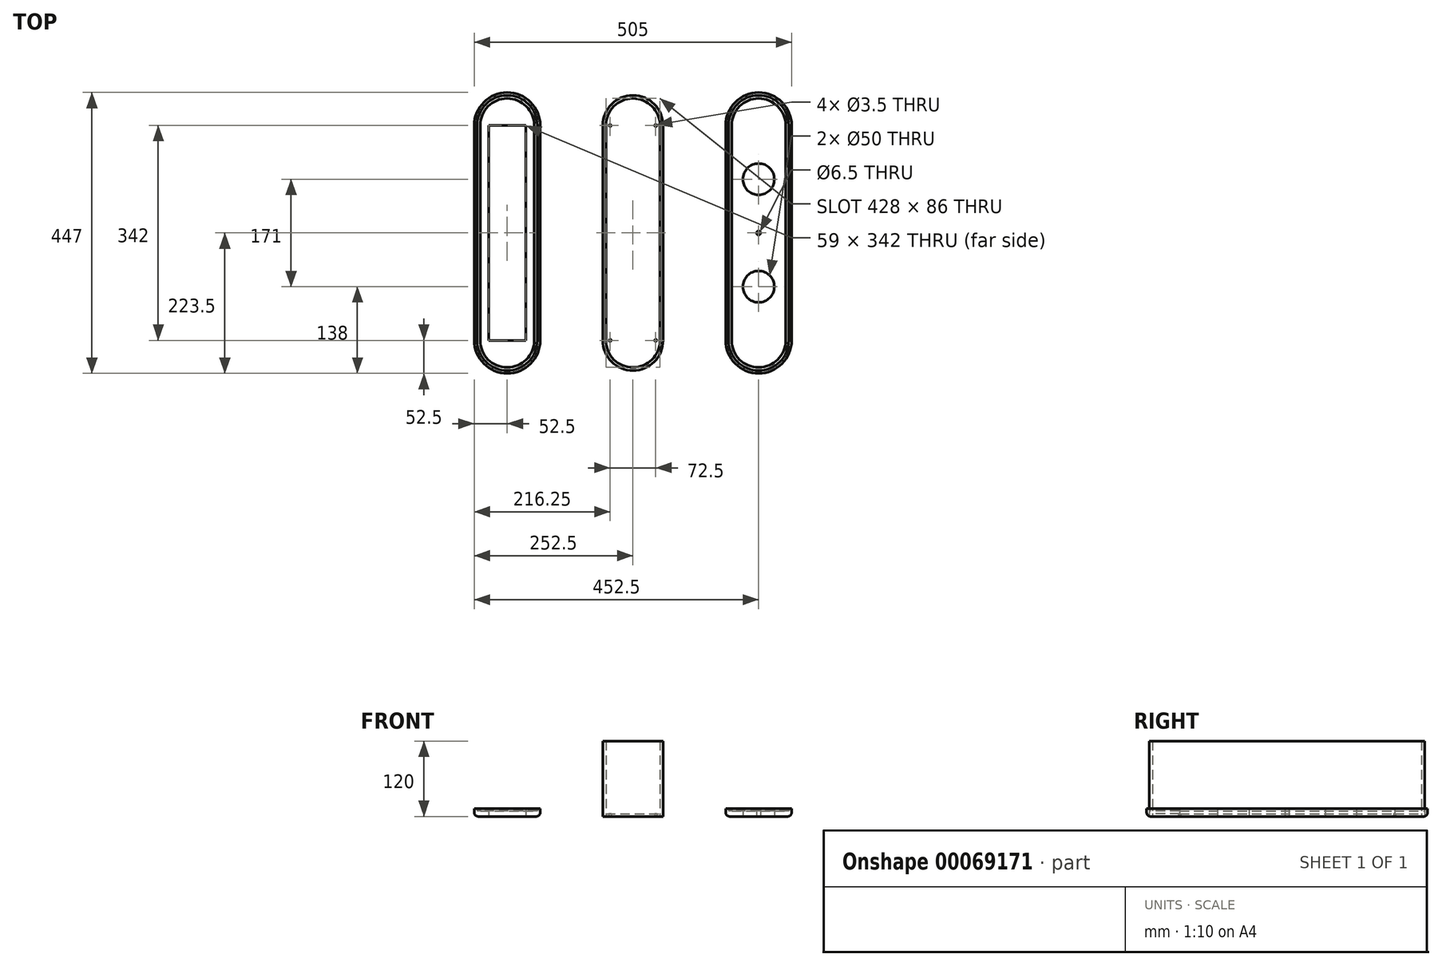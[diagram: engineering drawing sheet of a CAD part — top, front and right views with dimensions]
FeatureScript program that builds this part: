
annotation { "Feature Type Name" : "Feature", "Feature Type Description" : "" }
export const myFeature = defineFeature(function(context is Context, id is Id, definition is map)
    precondition{}
    {
        {
            assignVariable(context, id + "F0", {"name" : "MaterialThickness", "anyValue" : 12.7});
        }
        {
            assignVariable(context, id + "F1", {"name" : "SignHeight", "anyValue" : 120});
        }
        {
            assignVariable(context, id + "F2", {"name" : "SignThickness", "anyValue" : 4.5});
        }
        {
            var Q0;
            Q0=qCreatedBy(makeId("Top.planeOp"),FACE);
            var sketch = newSketch(context, id + "F3", { "sketchPlane" : qUnion([Q0])});
            skLineSegment(sketch, "E0", {"start": v(0, 0) * mm, "end": v(105, 0) * mm, "construction": true});
            skLineSegment(sketch, "E1", {"start": v(105, 0) * mm, "end": v(105, 171) * mm});
            skLineSegment(sketch, "E2", {"start": v(0, 0) * mm, "end": v(0, 171) * mm});
            skArc(sketch, "E3", {"start": v(105, 171) * mm, "mid": v(52.5, 223.5) * mm, "end": v(0, 171) * mm});
            skPoint(sketch, "E3.centerSnap0", {"position": v(52.5, 0) * mm});
            skLineSegment(sketch, "E4.0", {"start": v(100.5, 0) * mm, "end": v(100.5, 171) * mm});
            skArc(sketch, "E4.1", {"start": v(100.5, 171) * mm, "mid": v(52.5, 219) * mm, "end": v(4.5, 171) * mm});
            skLineSegment(sketch, "E4.2", {"start": v(4.5, 0) * mm, "end": v(4.5, 171) * mm});
            skLineSegment(sketch, "E5.0", {"start": v(9.5, 0) * mm, "end": v(9.5, 171) * mm});
            skArc(sketch, "E5.1", {"start": v(95.5, 171) * mm, "mid": v(52.5, 214) * mm, "end": v(9.5, 171) * mm});
            skLineSegment(sketch, "E5.2", {"start": v(95.5, 0) * mm, "end": v(95.5, 171) * mm});
            skArc(sketch, "E6.MirrorCS", {"start": v(95.5, -171) * mm, "mid": v(52.5, -214) * mm, "end": v(9.5, -171) * mm});
            skLineSegment(sketch, "E7.MirrorCS", {"start": v(105, 0) * mm, "end": v(105, -171) * mm});
            skArc(sketch, "E8.MirrorCS", {"start": v(100.5, -171) * mm, "mid": v(52.5, -219) * mm, "end": v(4.5, -171) * mm});
            skLineSegment(sketch, "E9.MirrorCS", {"start": v(4.5, 0) * mm, "end": v(4.5, -171) * mm});
            skLineSegment(sketch, "E10.MirrorCS", {"start": v(0, 0) * mm, "end": v(0, -171) * mm});
            skLineSegment(sketch, "E11.MirrorCS", {"start": v(9.5, 0) * mm, "end": v(9.5, -171) * mm});
            skArc(sketch, "E12.MirrorCS", {"start": v(105, -171) * mm, "mid": v(52.5, -223.5) * mm, "end": v(0, -171) * mm});
            skLineSegment(sketch, "E13.MirrorCS", {"start": v(95.5, 0) * mm, "end": v(95.5, -171) * mm});
            skLineSegment(sketch, "E14.MirrorCS", {"start": v(100.5, 0) * mm, "end": v(100.5, -171) * mm});
            skLineSegment(sketch, "E15", {"start": v(52.5, 171) * mm, "end": v(52.5, -171) * mm, "construction": true});
            skPoint(sketch, "E16", {"position": v(52.5, 85.5) * mm});
            skPoint(sketch, "E17.MirrorP", {"position": v(52.5, -85.5) * mm});
            skLineSegment(sketch, "E18.rect.bottom", {"start": v(82, 171) * mm, "end": v(23, 171) * mm});
            skLineSegment(sketch, "E18.rect.top", {"start": v(82, -171) * mm, "end": v(23, -171) * mm});
            skLineSegment(sketch, "E18.rect.left", {"start": v(82, 171) * mm, "end": v(82, -171) * mm});
            skLineSegment(sketch, "E18.rect.right", {"start": v(23, 171) * mm, "end": v(23, -171) * mm});
            skPoint(sketch, "E19", {"position": v(16.25, -171) * mm});
            skPoint(sketch, "E20.MirrorP", {"position": v(88.75, -171) * mm});
            skPoint(sketch, "E21.MirrorP", {"position": v(88.75, 171) * mm});
            skPoint(sketch, "E22.MirrorP", {"position": v(16.25, 171) * mm});
            skSolve(sketch);
        }
        {
            var Q0;
            {var subQ0=sQuery(id+"F3.wireOp",EDGE,"S4vBLkRr-qZBK-nAqC-RG6z-cKJkzYe95XTT");Q0=makeQuery(id+"F3.imprint","IMPRINT",FACE,{"disambiguationData":[TD([[makeQuery(id+"F3.imprint","IMPRINT",EDGE,{"derivedFrom":subQ0}),1.0]])]});}
            var Q1;
            {var subQ0=sQuery(id+"F3.wireOp",EDGE,"zH33Oyk7-acCO-qxZw-FpOp-6ZJnxs5qB4Y2");Q1=makeQuery(id+"F3.imprint","IMPRINT",FACE,{"disambiguationData":[TD([[makeQuery(id+"F3.imprint","IMPRINT",EDGE,{"derivedFrom":subQ0}),-1.0]])]});}
            var Q2;
            {var subQ0=sQuery(id+"F3.wireOp",EDGE,"VhilzIQP-kfQW-MNlP-IUHr-LsH6QfZYn0pK");Q2=makeQuery(id+"F3.imprint","IMPRINT",FACE,{"disambiguationData":[TD([[makeQuery(id+"F3.imprint","IMPRINT",EDGE,{"derivedFrom":subQ0}),1.0]])]});}
            var Q3;
            {var subQ4=sQuery(id+"F3.wireOp",EDGE,"E3");Q3=makeQuery(id+"F3.imprint","IMPRINT",FACE,{"disambiguationData":[TD([[makeQuery(id+"F3.imprint","IMPRINT",EDGE,{"derivedFrom":subQ4}),1.0]])]});}
            var Q4;
            Q4=makeQuery(id+"F3.imprint","IMPRINT",FACE,{"disambiguationData":[TD([[makeQuery(id+"F3.imprint","IMPRINT",EDGE,{"derivedFrom":sQuery(id+"F3.wireOp",EDGE,"E18.rect.bottom")}),1.0]])]});
            var Q5;
            Q5=makeQuery(id+"F3.imprint","IMPRINT",FACE,{"disambiguationData":[TD([[makeQuery(id+"F3.imprint","IMPRINT",EDGE,{"derivedFrom":sQuery(id+"F3.wireOp",EDGE,"E18.rect.bottom")}),-1.0]])]});
            var Q6;
            Q6=makeQuery(id+"F3.imprint","IMPRINT",FACE,{"disambiguationData":[TD([[makeQuery(id+"F3.imprint","IMPRINT",EDGE,{"derivedFrom":sQuery(id+"F3.wireOp",EDGE,"E5.0")}),-1.0]])]});
            extrude(context, id + "F4", {"entities" : qUnion([Q0, Q1, Q2, Q3, Q4, Q5, Q6]), "depth" : (getVariable(context, 'MaterialThickness')) * mm});
        }
        {
            var Q0;
            {var subQ0=sQuery(id+"F3.wireOp",EDGE,"yTFAeiCs-v25R-ZgTO-i8Xo-Mo7MgQb8BnxG");Q0=makeQuery(id+"F3.imprint","IMPRINT",FACE,{"disambiguationData":[TD([[makeQuery(id+"F3.imprint","IMPRINT",EDGE,{"derivedFrom":subQ0}),1.0]])]});}
            var Q1;
            {var subQ0=sQuery(id+"F3.wireOp",EDGE,"4b8e0ea6-be84-4a1c-8fd7-66489d5511090.MirrorCS");Q1=makeQuery(id+"F3.imprint","IMPRINT",FACE,{"disambiguationData":[TD([[makeQuery(id+"F3.imprint","IMPRINT",EDGE,{"derivedFrom":subQ0}),-1.0]])]});}
            var Q2;
            {var subQ4=sQuery(id+"F3.wireOp",EDGE,"E4.1");Q2=makeQuery(id+"F3.imprint","IMPRINT",FACE,{"disambiguationData":[TD([[makeQuery(id+"F3.imprint","IMPRINT",EDGE,{"derivedFrom":subQ4}),1.0]])]});}
            var Q3;
            {var subQ0=sQuery(id+"F3.wireOp",EDGE,"E2");var subQ1=sQuery(id+"F3.wireOp",EDGE,"E0");var subQ2=makeQuery(id+"F3.imprint","INTERSECT",VERTEX,{"derivedFrom":[subQ1,subQ0]});Q3=makeQuery(id+"F3.imprint","IMPRINT",FACE,{"disambiguationData":[TD([[makeQuery(id+"F3.imprint","IMPRINT",EDGE,{"disambiguationData":[TD([[subQ2,-1.0]])],"derivedFrom":subQ1}),1.0]])]});}
            var Q4;
            {var subQ0=sQuery(id+"F3.wireOp",EDGE,"E4.2");var subQ1=sQuery(id+"F3.wireOp",EDGE,"E0");var subQ2=makeQuery(id+"F3.imprint","INTERSECT",VERTEX,{"derivedFrom":[subQ1,subQ0]});Q4=makeQuery(id+"F3.imprint","IMPRINT",FACE,{"disambiguationData":[TD([[makeQuery(id+"F3.imprint","IMPRINT",EDGE,{"disambiguationData":[TD([[subQ2,-1.0]])],"derivedFrom":subQ1}),1.0]])]});}
            var Q5;
            {var subQ0=sQuery(id+"F3.wireOp",EDGE,"E5.0");var subQ1=sQuery(id+"F3.wireOp",EDGE,"E0");var subQ2=makeQuery(id+"F3.imprint","INTERSECT",VERTEX,{"derivedFrom":[subQ1,subQ0]});Q5=makeQuery(id+"F3.imprint","IMPRINT",FACE,{"disambiguationData":[TD([[makeQuery(id+"F3.imprint","IMPRINT",EDGE,{"disambiguationData":[TD([[subQ2,-1.0]])],"derivedFrom":subQ1}),1.0]])]});}
            var Q6;
            {var subQ0=sQuery(id+"F3.wireOp",EDGE,"E4.0");var subQ1=sQuery(id+"F3.wireOp",EDGE,"E0");var subQ2=makeQuery(id+"F3.imprint","INTERSECT",VERTEX,{"derivedFrom":[subQ1,subQ0]});Q6=makeQuery(id+"F3.imprint","IMPRINT",FACE,{"disambiguationData":[TD([[makeQuery(id+"F3.imprint","IMPRINT",EDGE,{"disambiguationData":[TD([[subQ2,1.0]])],"derivedFrom":subQ1}),1.0]])]});}
            var Q7;
            {var subQ0=sQuery(id+"F3.wireOp",EDGE,"E1");var subQ1=sQuery(id+"F3.wireOp",EDGE,"E0");var subQ2=makeQuery(id+"F3.imprint","INTERSECT",VERTEX,{"derivedFrom":[subQ1,subQ0]});Q7=makeQuery(id+"F3.imprint","IMPRINT",FACE,{"disambiguationData":[TD([[makeQuery(id+"F3.imprint","IMPRINT",EDGE,{"disambiguationData":[TD([[subQ2,1.0]])],"derivedFrom":subQ1}),1.0]])]});}
            var Q8;
            {var subQ0=sQuery(id+"F3.wireOp",EDGE,"CrX6ssRw-XUBs-B3EW-npsk-YDTcKUYaLTWO");var subQ1=sQuery(id+"F3.wireOp",EDGE,"E5.0");var subQ2=makeQuery(id+"F3.imprint","INTERSECT",VERTEX,{"derivedFrom":[subQ1,subQ0]});Q8=makeQuery(id+"F3.imprint","IMPRINT",FACE,{"disambiguationData":[TD([[makeQuery(id+"F3.imprint","IMPRINT",EDGE,{"disambiguationData":[TD([[subQ2,-1.0]])],"derivedFrom":subQ1}),-1.0]])]});}
            var Q9;
            {var subQ0=sQuery(id+"F3.wireOp",EDGE,"CrX6ssRw-XUBs-B3EW-npsk-YDTcKUYaLTWO");var subQ1=sQuery(id+"F3.wireOp",EDGE,"E4.2");var subQ2=makeQuery(id+"F3.imprint","INTERSECT",VERTEX,{"derivedFrom":[subQ1,subQ0]});Q9=makeQuery(id+"F3.imprint","IMPRINT",FACE,{"disambiguationData":[TD([[makeQuery(id+"F3.imprint","IMPRINT",EDGE,{"disambiguationData":[TD([[subQ2,-1.0]])],"derivedFrom":subQ1}),-1.0]])]});}
            var Q10;
            {var subQ0=sQuery(id+"F3.wireOp",EDGE,"CrX6ssRw-XUBs-B3EW-npsk-YDTcKUYaLTWO");var subQ1=sQuery(id+"F3.wireOp",EDGE,"E4.0");var subQ2=makeQuery(id+"F3.imprint","INTERSECT",VERTEX,{"derivedFrom":[subQ1,subQ0]});Q10=makeQuery(id+"F3.imprint","IMPRINT",FACE,{"disambiguationData":[TD([[makeQuery(id+"F3.imprint","IMPRINT",EDGE,{"disambiguationData":[TD([[subQ2,-1.0]])],"derivedFrom":subQ1}),1.0]])]});}
            extrude(context, id + "F5", {"entities" : qUnion([Q0, Q1, Q2, Q3, Q4, Q5, Q6, Q7, Q8, Q9, Q10]), "operationType" : NewBodyOperationType.ADD, "depth" : (getVariable(context, 'MaterialThickness') * 2 / 3) * mm});
        }
        {
            var Q0;
            Q0=sQuery(id+"F3.wireOp",VERTEX,"E17.MirrorP");
            var Q1;
            Q1=sQuery(id+"F3.wireOp",VERTEX,"E16");
            var Q2;
            Q2=makeQuery(id+"F4.opExtrude","SWEPT_BODY",BODY,{"disambiguationData":[OSD([sQuery(id+"F3.wireOp",EDGE,"E1"),sQuery(id+"F3.wireOp",EDGE,"E2"),sQuery(id+"F3.wireOp",EDGE,"E3"),sQuery(id+"F3.wireOp",EDGE,"E4.0"),sQuery(id+"F3.wireOp",EDGE,"E4.1"),sQuery(id+"F3.wireOp",EDGE,"E4.2"),sQuery(id+"F3.wireOp",EDGE,"E7.MirrorCS"),sQuery(id+"F3.wireOp",EDGE,"E8.MirrorCS"),sQuery(id+"F3.wireOp",EDGE,"E9.MirrorCS"),sQuery(id+"F3.wireOp",EDGE,"E10.MirrorCS"),sQuery(id+"F3.wireOp",EDGE,"E12.MirrorCS"),sQuery(id+"F3.wireOp",EDGE,"E14.MirrorCS")])]});
            hole(context, id + "F6", {"style" : HoleStyle.SIMPLE, "holeDiameter" : 50 * mm, "endStyle" : HoleEndStyle.THROUGH, "oppositeDirection" : true, "locations" : qUnion([Q0, Q1]), "scope" : qUnion([Q2])});
        }
        {
            var Q0;
            Q0=sQuery(id+"F3.wireOp",VERTEX,"E3.centerSnap0");
            var Q1;
            Q1=makeQuery(id+"F4.opExtrude","SWEPT_BODY",BODY,{"disambiguationData":[OSD([sQuery(id+"F3.wireOp",EDGE,"E1"),sQuery(id+"F3.wireOp",EDGE,"E2"),sQuery(id+"F3.wireOp",EDGE,"E3"),sQuery(id+"F3.wireOp",EDGE,"E4.0"),sQuery(id+"F3.wireOp",EDGE,"E4.1"),sQuery(id+"F3.wireOp",EDGE,"E4.2"),sQuery(id+"F3.wireOp",EDGE,"E7.MirrorCS"),sQuery(id+"F3.wireOp",EDGE,"E8.MirrorCS"),sQuery(id+"F3.wireOp",EDGE,"E9.MirrorCS"),sQuery(id+"F3.wireOp",EDGE,"E10.MirrorCS"),sQuery(id+"F3.wireOp",EDGE,"E12.MirrorCS"),sQuery(id+"F3.wireOp",EDGE,"E14.MirrorCS")])]});
            hole(context, id + "F7", {"style" : HoleStyle.SIMPLE, "holeDiameter" : 6.5 * mm, "endStyle" : HoleEndStyle.THROUGH, "oppositeDirection" : true, "locations" : qUnion([Q0]), "scope" : qUnion([Q1])});
        }
        {
            var Q0;
            Q0=makeQuery(id+"F4.opExtrude","SWEPT_BODY",BODY,{"disambiguationData":[OSD([sQuery(id+"F3.wireOp",EDGE,"E1"),sQuery(id+"F3.wireOp",EDGE,"E2"),sQuery(id+"F3.wireOp",EDGE,"E3"),sQuery(id+"F3.wireOp",EDGE,"E4.0"),sQuery(id+"F3.wireOp",EDGE,"E4.1"),sQuery(id+"F3.wireOp",EDGE,"E4.2"),sQuery(id+"F3.wireOp",EDGE,"E7.MirrorCS"),sQuery(id+"F3.wireOp",EDGE,"E8.MirrorCS"),sQuery(id+"F3.wireOp",EDGE,"E9.MirrorCS"),sQuery(id+"F3.wireOp",EDGE,"E10.MirrorCS"),sQuery(id+"F3.wireOp",EDGE,"E12.MirrorCS"),sQuery(id+"F3.wireOp",EDGE,"E14.MirrorCS")])]});
            transform(context, id + "F8", {"entities" : qUnion([Q0]), "transformType" : TransformType.TRANSLATION_3D, "dx" : 200 * mm, "dy" : 0 * mm, "dz" : 0 * mm, "makeCopy" : false});
        }
        {
            var Q0;
            Q0=makeQuery(id+"F3.imprint","IMPRINT",FACE,{"disambiguationData":[TD([[makeQuery(id+"F3.imprint","IMPRINT",EDGE,{"derivedFrom":sQuery(id+"F3.wireOp",EDGE,"E1")}),1.0]])]});
            var Q1;
            Q1=makeQuery(id+"F3.imprint","IMPRINT",FACE,{"disambiguationData":[TD([[makeQuery(id+"F3.imprint","IMPRINT",EDGE,{"derivedFrom":sQuery(id+"F3.wireOp",EDGE,"E5.0")}),-1.0]])]});
            var Q2;
            Q2=makeQuery(id+"F3.imprint","IMPRINT",FACE,{"disambiguationData":[TD([[makeQuery(id+"F3.imprint","IMPRINT",EDGE,{"derivedFrom":sQuery(id+"F3.wireOp",EDGE,"E18.rect.bottom")}),-1.0]])]});
            extrude(context, id + "F9", {"entities" : qUnion([Q0, Q1, Q2]), "depth" : (getVariable(context, 'MaterialThickness')) * mm});
        }
        {
            var Q0;
            Q0=makeQuery(id+"F3.imprint","IMPRINT",FACE,{"disambiguationData":[TD([[makeQuery(id+"F3.imprint","IMPRINT",EDGE,{"derivedFrom":sQuery(id+"F3.wireOp",EDGE,"E4.0")}),1.0]])]});
            extrude(context, id + "F10", {"entities" : qUnion([Q0]), "operationType" : NewBodyOperationType.ADD, "depth" : (getVariable(context, 'MaterialThickness') * 2 / 3) * mm});
        }
        {
            var Q0;
            Q0=makeQuery(id+"F9.opExtrude","SWEPT_BODY",BODY,{"disambiguationData":[OSD([sQuery(id+"F3.wireOp",EDGE,"E1"),sQuery(id+"F3.wireOp",EDGE,"E2"),sQuery(id+"F3.wireOp",EDGE,"E3"),sQuery(id+"F3.wireOp",EDGE,"E4.0"),sQuery(id+"F3.wireOp",EDGE,"E4.1"),sQuery(id+"F3.wireOp",EDGE,"E4.2"),sQuery(id+"F3.wireOp",EDGE,"E7.MirrorCS"),sQuery(id+"F3.wireOp",EDGE,"E8.MirrorCS"),sQuery(id+"F3.wireOp",EDGE,"E9.MirrorCS"),sQuery(id+"F3.wireOp",EDGE,"E10.MirrorCS"),sQuery(id+"F3.wireOp",EDGE,"E12.MirrorCS"),sQuery(id+"F3.wireOp",EDGE,"E14.MirrorCS")])]});
            transform(context, id + "F11", {"entities" : qUnion([Q0]), "transformType" : TransformType.TRANSLATION_3D, "dx" : -200 * mm, "dy" : 0 * mm, "dz" : 0 * mm, "makeCopy" : false});
        }
        {
            var Q0;
            {var subQ0=sQuery(id+"F3.wireOp",EDGE,"6601b8a4-b0c0-4b59-8abf-b862b479d69b.trimOffspring");Q0=makeQuery(id+"F3.imprint","IMPRINT",FACE,{"disambiguationData":[TD([[makeQuery(id+"F3.imprint","IMPRINT",EDGE,{"derivedFrom":subQ0}),1.0]])]});}
            var Q1;
            {var subQ1=sQuery(id+"F3.wireOp",EDGE,"E4.1");Q1=makeQuery(id+"F3.imprint","IMPRINT",FACE,{"disambiguationData":[TD([[makeQuery(id+"F3.imprint","IMPRINT",EDGE,{"derivedFrom":subQ1}),1.0]])]});}
            var Q2;
            {var subQ1=sQuery(id+"F3.wireOp",EDGE,"E4.1");Q2=makeQuery(id+"F3.imprint","IMPRINT",FACE,{"disambiguationData":[TD([[makeQuery(id+"F3.imprint","IMPRINT",EDGE,{"derivedFrom":subQ1}),1.0]])]});}
            extrude(context, id + "F12", {"entities" : qUnion([Q0, Q1, Q2]), "depth" : (getVariable(context, 'SignHeight')) * mm});
        }
        {
            var Q0;
            Q0=makeQuery(id+"F3.imprint","IMPRINT",FACE,{"disambiguationData":[TD([[makeQuery(id+"F3.imprint","IMPRINT",EDGE,{"derivedFrom":sQuery(id+"F3.wireOp",EDGE,"E5.0")}),-1.0]])]});
            var Q1;
            Q1=makeQuery(id+"F3.imprint","IMPRINT",FACE,{"disambiguationData":[TD([[makeQuery(id+"F3.imprint","IMPRINT",EDGE,{"derivedFrom":sQuery(id+"F3.wireOp",EDGE,"E18.rect.bottom")}),1.0]])]});
            extrude(context, id + "F13", {"entities" : qUnion([Q0, Q1]), "depth" : (getVariable(context, 'SignThickness')) * mm});
        }
        {
            var Q0;
            Q0=sQuery(id+"F3.wireOp",VERTEX,"E19");
            var Q1;
            Q1=sQuery(id+"F3.wireOp",VERTEX,"E20.MirrorP");
            var Q2;
            Q2=sQuery(id+"F3.wireOp",VERTEX,"E22.MirrorP");
            var Q3;
            Q3=sQuery(id+"F3.wireOp",VERTEX,"E21.MirrorP");
            var Q4;
            Q4=makeQuery(id+"F13.opExtrude","SWEPT_BODY",BODY,{"disambiguationData":[OSD([sQuery(id+"F3.wireOp",EDGE,"E5.0"),sQuery(id+"F3.wireOp",EDGE,"E5.1"),sQuery(id+"F3.wireOp",EDGE,"E5.2"),sQuery(id+"F3.wireOp",EDGE,"E6.MirrorCS"),sQuery(id+"F3.wireOp",EDGE,"E11.MirrorCS"),sQuery(id+"F3.wireOp",EDGE,"E13.MirrorCS")])]});
            hole(context, id + "F14", {"style" : HoleStyle.SIMPLE, "holeDiameter" : 3.5 * mm, "endStyle" : HoleEndStyle.THROUGH, "oppositeDirection" : true, "locations" : qUnion([Q0, Q1, Q2, Q3]), "scope" : qUnion([Q4])});
        }
        {
            var Q0;
            {var subQ0=sQuery(id+"F3.wireOp",EDGE,"E2");Q0=makeQuery(id+"F5.boolean.opBoolean","MERGE",EDGE,{"derivedFrom":[makeQuery(id+"F4.opExtrude","CAP_EDGE",EDGE,{"disambiguationData":[OSD([subQ0])],"isStart":true}),makeQuery(id+"F5.opExtrude","CAP_EDGE",EDGE,{"disambiguationData":[OSD([subQ0])],"isStart":true})]});}
            var Q1;
            Q1=makeQuery(id+"F9.opExtrude","CAP_EDGE",EDGE,{"disambiguationData":[OSD([sQuery(id+"F3.wireOp",EDGE,"E1"),sQuery(id+"F3.wireOp",EDGE,"E7.MirrorCS")])],"isStart":true});
            fillet(context, id + "F15", {"entities" : qUnion([Q0, Q1]), "radius" : 6.35 * mm, "tangentPropagation" : true, "allowEdgeOverflow" : false});
        }
    });
